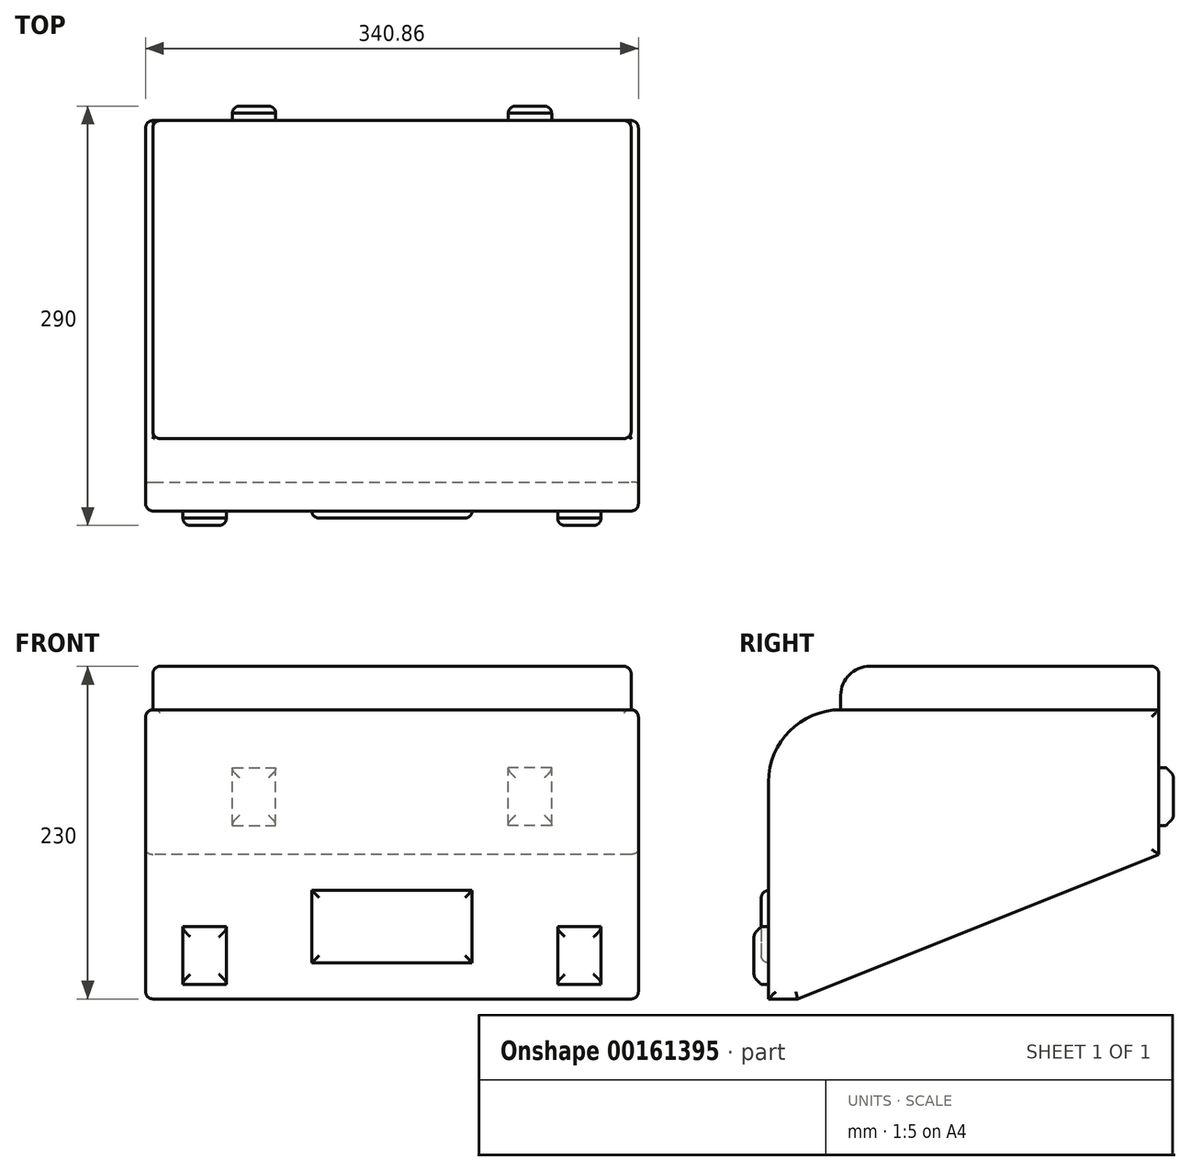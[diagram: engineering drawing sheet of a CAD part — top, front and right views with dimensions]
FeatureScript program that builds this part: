
annotation { "Feature Type Name" : "Feature", "Feature Type Description" : "" }
export const myFeature = defineFeature(function(context is Context, id is Id, definition is map)
    precondition{}
    {
        {
            var Q0;
            Q0=qCreatedBy(makeId("Top.planeOp"),FACE);
            var sketch = newSketch(context, id + "F0", { "sketchPlane" : qUnion([Q0])});
            skLineSegment(sketch, "E0.bottom", {"start": v(-169.57, 181.05) * mm, "end": v(170.43, 181.05) * mm});
            skLineSegment(sketch, "E0.top", {"start": v(-169.57, -88.95) * mm, "end": v(170.43, -88.95) * mm});
            skLineSegment(sketch, "E0.left", {"start": v(-169.57, 181.05) * mm, "end": v(-169.57, -88.95) * mm});
            skLineSegment(sketch, "E0.right", {"start": v(170.43, 181.05) * mm, "end": v(170.43, -88.95) * mm});
            skSolve(sketch);
        }
        {
            var Q0;
            Q0 = qSketchRegion(id + "F0", true);
            extrude(context, id + "F1", {"entities" : qUnion([Q0]), "depth" : 200 * mm});
        }
        {
            var Q0;
            Q0=makeQuery(id+"F1.opExtrude","CAP_EDGE",EDGE,{"disambiguationData":[OSD([sQuery(id+"F0.wireOp",EDGE,"E0.bottom")])],"isStart":true});
            chamfer(context, id + "F2", {"entities" : qUnion([Q0]), "chamferType" : ChamferType.TWO_OFFSETS, "width1" : 250 * mm, "oppositeDirection" : false, "width2" : 100 * mm, "tangentPropagation" : true});
        }
        {
            var Q0;
            Q0=makeQuery(id+"F1.opExtrude","CAP_EDGE",EDGE,{"disambiguationData":[OSD([sQuery(id+"F0.wireOp",EDGE,"E0.top")])],"isStart":false});
            fillet(context, id + "F3", {"entities" : qUnion([Q0]), "radius" : 50 * mm, "tangentPropagation" : true, "allowEdgeOverflow" : false});
        }
        {
            var Q0;
            Q0=makeQuery(id+"F2.opChamfer","BLEND_EDGE",EDGE,{"blendedFrom":[makeQuery(id+"F1.opExtrude","CAP_EDGE",EDGE,{"disambiguationData":[OSD([sQuery(id+"F0.wireOp",EDGE,"E0.bottom")])],"isStart":true}),makeQuery(id+"F1.opExtrude","SWEPT_FACE",FACE,{"disambiguationData":[OSD([sQuery(id+"F0.wireOp",EDGE,"E0.left")])]})],"blendedInto":[makeQuery(id+"F1.opExtrude","SWEPT_FACE",FACE,{"disambiguationData":[OSD([sQuery(id+"F0.wireOp",EDGE,"E0.left")])]})]});
            var Q1;
            Q1=makeQuery(id+"F1.opExtrude","SWEPT_FACE",FACE,{"disambiguationData":[OSD([sQuery(id+"F0.wireOp",EDGE,"E0.left")])]});
            fillet(context, id + "F4", {"entities" : qUnion([Q0, Q1]), "radius" : 5 * mm, "tangentPropagation" : true, "allowEdgeOverflow" : false});
        }
        {
            var Q0;
            Q0=makeQuery(id+"F1.opExtrude","SWEPT_FACE",FACE,{"disambiguationData":[OSD([sQuery(id+"F0.wireOp",EDGE,"E0.right")])]});
            fillet(context, id + "F5", {"entities" : qUnion([Q0]), "radius" : 5 * mm, "tangentPropagation" : true, "allowEdgeOverflow" : false});
        }
        {
            var Q0;
            Q0=makeQuery(id+"F1.opExtrude","SWEPT_FACE",FACE,{"disambiguationData":[OSD([sQuery(id+"F0.wireOp",EDGE,"E0.top")])]});
            var sketch = newSketch(context, id + "F6", { "sketchPlane" : qUnion([Q0])});
            skLineSegment(sketch, "E1.bottom", {"start": v(-44.57, 75) * mm, "end": v(55.43, 75) * mm});
            skLineSegment(sketch, "E1.top", {"start": v(-44.57, 25) * mm, "end": v(55.43, 25) * mm});
            skLineSegment(sketch, "E1.left", {"start": v(-44.57, 75) * mm, "end": v(-44.57, 25) * mm});
            skLineSegment(sketch, "E1.right", {"start": v(55.43, 75) * mm, "end": v(55.43, 25) * mm});
            skSolve(sketch);
        }
        {
            var Q0;
            Q0 = qSketchRegion(id + "F6", true);
            extrude(context, id + "F7", {"entities" : qUnion([Q0]), "operationType" : NewBodyOperationType.ADD, "depth" : 5 * mm});
        }
        {
            var Q0;
            Q0=makeQuery(id+"F7.opExtrude","CAP_FACE",FACE,{"disambiguationData":[OSD([sQuery(id+"F6.wireOp",EDGE,"E1.bottom"),sQuery(id+"F6.wireOp",EDGE,"E1.top"),sQuery(id+"F6.wireOp",EDGE,"E1.left"),sQuery(id+"F6.wireOp",EDGE,"E1.right")])],"isStart":false});
            fillet(context, id + "F8", {"entities" : qUnion([Q0]), "radius" : 5 * mm, "tangentPropagation" : true, "allowEdgeOverflow" : false});
        }
        {
            var Q0;
            Q0=makeQuery(id+"F1.opExtrude","CAP_FACE",FACE,{"disambiguationData":[OSD([sQuery(id+"F0.wireOp",EDGE,"E0.bottom"),sQuery(id+"F0.wireOp",EDGE,"E0.top"),sQuery(id+"F0.wireOp",EDGE,"E0.left"),sQuery(id+"F0.wireOp",EDGE,"E0.right")])],"isStart":false});
            var sketch = newSketch(context, id + "F9", { "sketchPlane" : qUnion([Q0])});
            skLineSegment(sketch, "E2.bottom", {"start": v(-164.57, 181.05) * mm, "end": v(165.43, 181.05) * mm});
            skLineSegment(sketch, "E2.top", {"start": v(-164.57, -38.95) * mm, "end": v(165.43, -38.95) * mm});
            skLineSegment(sketch, "E2.left", {"start": v(-164.57, 181.05) * mm, "end": v(-164.57, -38.95) * mm});
            skLineSegment(sketch, "E2.right", {"start": v(165.43, 181.05) * mm, "end": v(165.43, -38.95) * mm});
            skSolve(sketch);
        }
        {
            var Q0;
            Q0 = qSketchRegion(id + "F9", true);
            extrude(context, id + "F10", {"entities" : qUnion([Q0]), "operationType" : NewBodyOperationType.ADD, "depth" : 30 * mm});
        }
        {
            var Q0;
            Q0=makeQuery(id+"F10.opExtrude","CAP_EDGE",EDGE,{"disambiguationData":[OSD([sQuery(id+"F9.wireOp",EDGE,"E2.top")])],"isStart":false});
            fillet(context, id + "F11", {"entities" : qUnion([Q0]), "radius" : 20 * mm, "tangentPropagation" : true, "allowEdgeOverflow" : false});
        }
        {
            var Q0;
            Q0=makeQuery(id+"F10.opExtrude","CAP_FACE",FACE,{"disambiguationData":[OSD([sQuery(id+"F9.wireOp",EDGE,"E2.bottom"),sQuery(id+"F9.wireOp",EDGE,"E2.top"),sQuery(id+"F9.wireOp",EDGE,"E2.left"),sQuery(id+"F9.wireOp",EDGE,"E2.right")])],"isStart":false});
            fillet(context, id + "F12", {"entities" : qUnion([Q0]), "radius" : 5 * mm, "tangentPropagation" : true, "allowEdgeOverflow" : false});
        }
        {
            var Q0;
            Q0=makeQuery(id+"F10.opExtrude","SWEPT_EDGE",EDGE,{"disambiguationData":[OSD([sQuery(id+"F9.wireOp",EDGE,"E2.bottom"),sQuery(id+"F9.wireOp",EDGE,"E2.left")])]});
            fillet(context, id + "F13", {"entities" : qUnion([Q0]), "radius" : 5 * mm, "tangentPropagation" : true, "allowEdgeOverflow" : false});
        }
        {
            var Q0;
            Q0=makeQuery(id+"F10.opExtrude","SWEPT_EDGE",EDGE,{"disambiguationData":[OSD([sQuery(id+"F9.wireOp",EDGE,"E2.bottom"),sQuery(id+"F9.wireOp",EDGE,"E2.right")])]});
            fillet(context, id + "F14", {"entities" : qUnion([Q0]), "radius" : 5 * mm, "tangentPropagation" : true, "allowEdgeOverflow" : false});
        }
        {
            var Q0;
            Q0=makeQuery(id+"F1.opExtrude","SWEPT_FACE",FACE,{"disambiguationData":[OSD([sQuery(id+"F0.wireOp",EDGE,"E0.top")])]});
            var sketch = newSketch(context, id + "F15", { "sketchPlane" : qUnion([Q0])});
            skLineSegment(sketch, "E3.bottom", {"start": v(-144.57, 50) * mm, "end": v(-114.57, 50) * mm});
            skLineSegment(sketch, "E3.top", {"start": v(-144.57, 10) * mm, "end": v(-114.57, 10) * mm});
            skLineSegment(sketch, "E3.left", {"start": v(-144.57, 50) * mm, "end": v(-144.57, 10) * mm});
            skLineSegment(sketch, "E3.right", {"start": v(-114.57, 50) * mm, "end": v(-114.57, 10) * mm});
            skSolve(sketch);
        }
        {
            var Q0;
            Q0 = qSketchRegion(id + "F15", true);
            extrude(context, id + "F16", {"entities" : qUnion([Q0]), "operationType" : NewBodyOperationType.ADD, "depth" : 10 * mm});
        }
        {
            var Q0;
            Q0=makeQuery(id+"F16.opExtrude","CAP_EDGE",EDGE,{"disambiguationData":[OSD([sQuery(id+"F15.wireOp",EDGE,"E3.bottom")])],"isStart":false});
            var Q1;
            Q1=makeQuery(id+"F16.opExtrude","CAP_EDGE",EDGE,{"disambiguationData":[OSD([sQuery(id+"F15.wireOp",EDGE,"E3.top")])],"isStart":false});
            chamfer(context, id + "F17", {"entities" : qUnion([Q0, Q1]), "width" : 5 * mm, "tangentPropagation" : true});
        }
        {
            var Q0;
            Q0=makeQuery(id+"F16.opExtrude","CAP_FACE",FACE,{"disambiguationData":[OSD([sQuery(id+"F15.wireOp",EDGE,"E3.bottom"),sQuery(id+"F15.wireOp",EDGE,"E3.top"),sQuery(id+"F15.wireOp",EDGE,"E3.left"),sQuery(id+"F15.wireOp",EDGE,"E3.right")])],"isStart":false});
            fillet(context, id + "F18", {"entities" : qUnion([Q0]), "radius" : 5 * mm, "tangentPropagation" : true, "allowEdgeOverflow" : false});
        }
        {
            var Q0;
            Q0=makeQuery(id+"F1.opExtrude","SWEPT_BODY",BODY,{"disambiguationData":[OSD([sQuery(id+"F0.wireOp",EDGE,"E0.bottom"),sQuery(id+"F0.wireOp",EDGE,"E0.top"),sQuery(id+"F0.wireOp",EDGE,"E0.left"),sQuery(id+"F0.wireOp",EDGE,"E0.right")])]});
            var Q1;
            Q1=qCreatedBy(makeId("Right.planeOp"),FACE);
            mirror(context, id + "F19", {"operationType" : NewBodyOperationType.ADD, "entities" : qUnion([Q0]), "mirrorPlane" : qUnion([Q1])});
        }
        {
            var Q0;
            {var subQ0=makeQuery(id+"F10.boolean.opBoolean","MERGE",FACE,{"derivedFrom":[makeQuery(id+"F1.opExtrude","SWEPT_FACE",FACE,{"disambiguationData":[OSD([sQuery(id+"F0.wireOp",EDGE,"E0.bottom")])]}),makeQuery(id+"F10.opExtrude","SWEPT_FACE",FACE,{"disambiguationData":[OSD([sQuery(id+"F9.wireOp",EDGE,"E2.bottom")])]})]});Q0=makeQuery(id+"F19.boolean.opBoolean","MERGE",FACE,{"derivedFrom":[subQ0,makeQuery(id+"F19.opPattern","COPY",FACE,{"derivedFrom":subQ0,"instanceName":"1"})]});}
            var sketch = newSketch(context, id + "F20", { "sketchPlane" : qUnion([Q0])});
            skLineSegment(sketch, "E4.bottom", {"start": v(-110.43, 120) * mm, "end": v(-80.43, 120) * mm});
            skLineSegment(sketch, "E4.top", {"start": v(-110.43, 160) * mm, "end": v(-80.43, 160) * mm});
            skLineSegment(sketch, "E4.left", {"start": v(-110.43, 120) * mm, "end": v(-110.43, 160) * mm});
            skLineSegment(sketch, "E4.right", {"start": v(-80.43, 120) * mm, "end": v(-80.43, 160) * mm});
            skSolve(sketch);
        }
        {
            var Q0;
            Q0 = qSketchRegion(id + "F20", true);
            extrude(context, id + "F21", {"entities" : qUnion([Q0]), "operationType" : NewBodyOperationType.ADD, "depth" : 10 * mm});
        }
        {
            var Q0;
            Q0=makeQuery(id+"F21.opExtrude","CAP_EDGE",EDGE,{"disambiguationData":[OSD([sQuery(id+"F20.wireOp",EDGE,"E4.top")])],"isStart":false});
            var Q1;
            Q1=makeQuery(id+"F21.opExtrude","CAP_EDGE",EDGE,{"disambiguationData":[OSD([sQuery(id+"F20.wireOp",EDGE,"E4.bottom")])],"isStart":false});
            chamfer(context, id + "F22", {"entities" : qUnion([Q0, Q1]), "width" : 5 * mm, "tangentPropagation" : true});
        }
        {
            var Q0;
            Q0=makeQuery(id+"F21.opExtrude","CAP_FACE",FACE,{"disambiguationData":[OSD([sQuery(id+"F20.wireOp",EDGE,"E4.bottom"),sQuery(id+"F20.wireOp",EDGE,"E4.top"),sQuery(id+"F20.wireOp",EDGE,"E4.left"),sQuery(id+"F20.wireOp",EDGE,"E4.right")])],"isStart":false});
            fillet(context, id + "F23", {"entities" : qUnion([Q0]), "radius" : 5 * mm, "tangentPropagation" : true, "allowEdgeOverflow" : false});
        }
        {
            var Q0;
            Q0=makeQuery(id+"F1.opExtrude","SWEPT_BODY",BODY,{"disambiguationData":[OSD([sQuery(id+"F0.wireOp",EDGE,"E0.bottom"),sQuery(id+"F0.wireOp",EDGE,"E0.top"),sQuery(id+"F0.wireOp",EDGE,"E0.left"),sQuery(id+"F0.wireOp",EDGE,"E0.right")])]});
            var Q1;
            Q1=qCreatedBy(makeId("Right.planeOp"),FACE);
            mirror(context, id + "F24", {"operationType" : NewBodyOperationType.ADD, "entities" : qUnion([Q0]), "mirrorPlane" : qUnion([Q1])});
        }
    });
